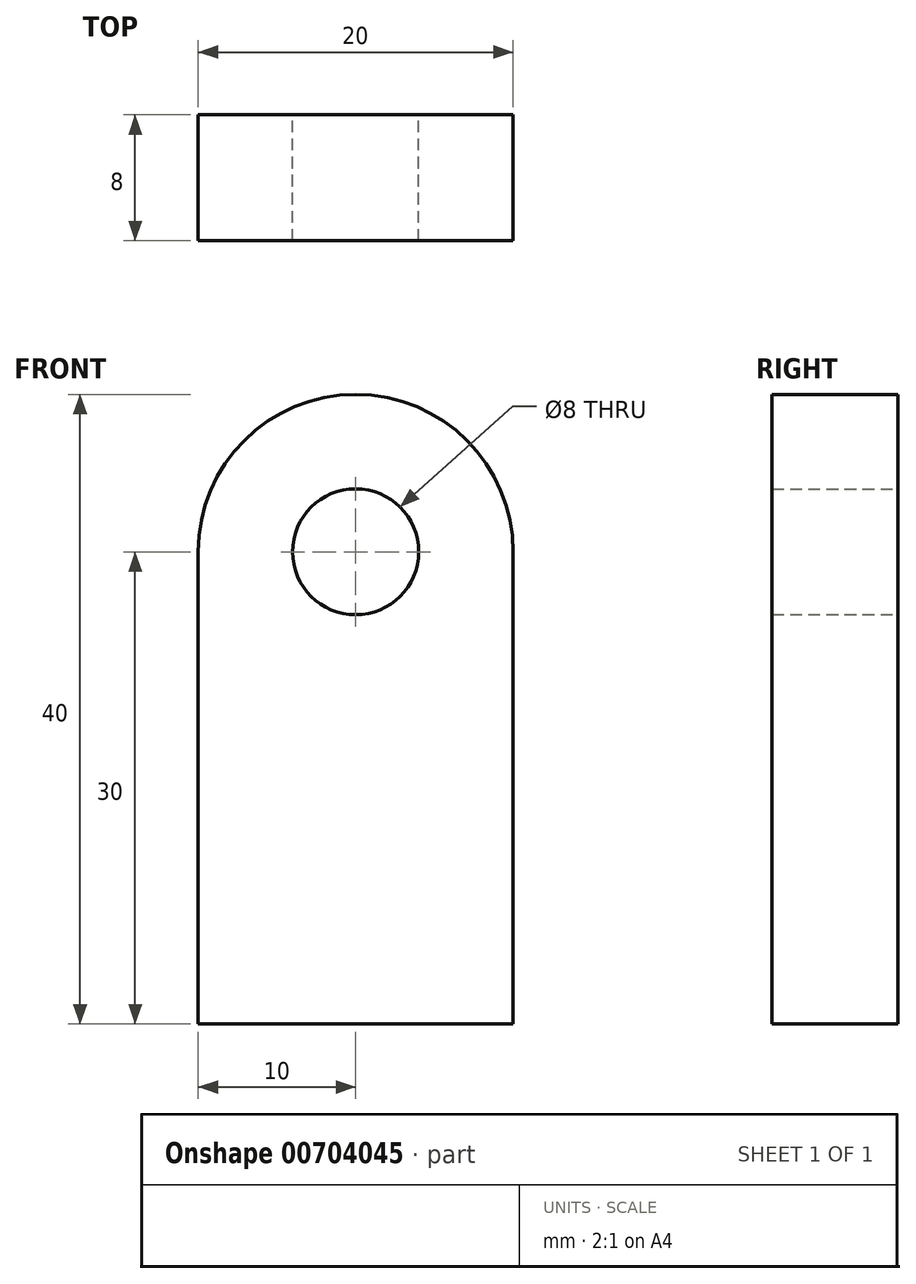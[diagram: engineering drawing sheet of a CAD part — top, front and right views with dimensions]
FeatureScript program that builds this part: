
annotation { "Feature Type Name" : "Feature", "Feature Type Description" : "" }
export const myFeature = defineFeature(function(context is Context, id is Id, definition is map)
    precondition{}
    {
        {
            var Q0;
            Q0=qCreatedBy(makeId("Front.planeOp"),FACE);
            var sketch = newSketch(context, id + "F0", { "sketchPlane" : qUnion([Q0])});
            skLineSegment(sketch, "E0", {"start": v(-10, 0) * mm, "end": v(10, 0) * mm});
            skCircle(sketch, "E1", {"center": v(0, 30) * mm, "radius": 4 * mm});
            skArc(sketch, "E2", {"start": v(10, 30) * mm, "mid": v(0, 40) * mm, "end": v(-10, 30) * mm});
            skLineSegment(sketch, "E3", {"start": v(-10, 0) * mm, "end": v(-10, 30) * mm});
            skLineSegment(sketch, "E4", {"start": v(10, 0) * mm, "end": v(10, 30) * mm});
            skSolve(sketch);
        }
        {
            var Q0;
            Q0=makeQuery(id+"F0.imprint","IMPRINT",FACE,{"disambiguationData":[TD([[makeQuery(id+"F0.imprint","IMPRINT",EDGE,{"derivedFrom":sQuery(id+"F0.wireOp",EDGE,"E0")}),1.0]])]});
            extrude(context, id + "F1", {"entities" : qUnion([Q0]), "depth" : 8 * mm, "offsetDistance" : 25.4 * mm});
        }
    });
